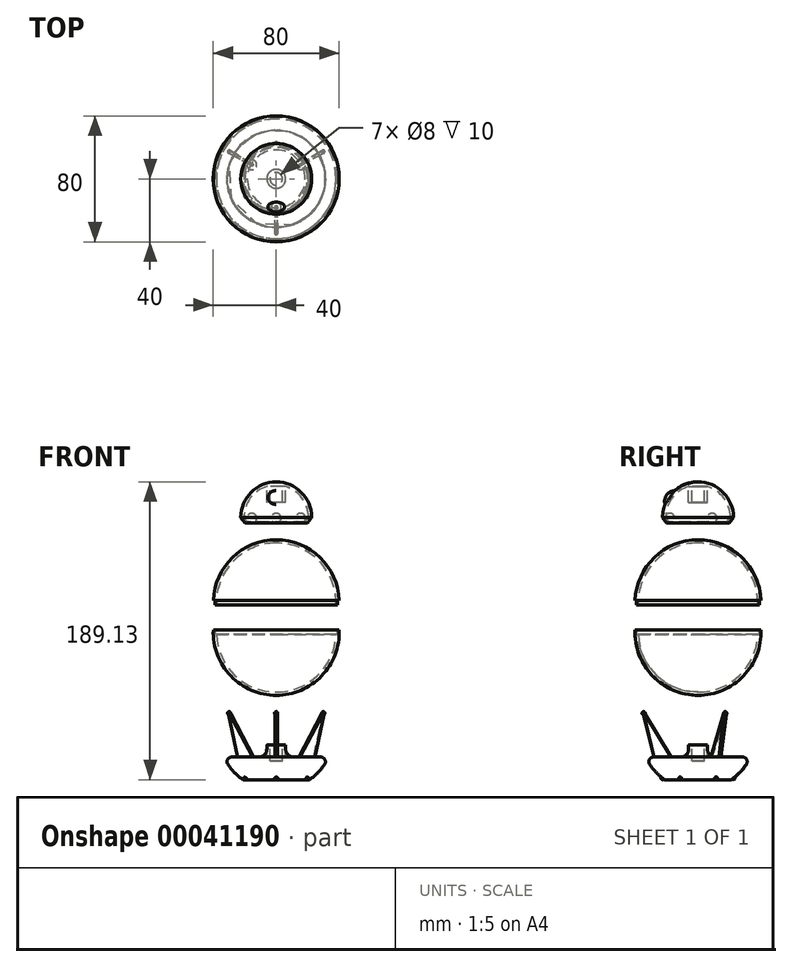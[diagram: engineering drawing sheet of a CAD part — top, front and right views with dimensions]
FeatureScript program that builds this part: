
annotation { "Feature Type Name" : "Feature", "Feature Type Description" : "" }
export const myFeature = defineFeature(function(context is Context, id is Id, definition is map)
    precondition{}
    {
        {
            var Q0;
            Q0=qCreatedBy(makeId("Right.planeOp"),FACE);
            var sketch = newSketch(context, id + "F0", { "sketchPlane" : qUnion([Q0])});
            skArc(sketch, "E0", {"start": v(0, 22.5) * mm, "mid": v(-15.9, 15.9) * mm, "end": v(-22.5, 0) * mm});
            skArc(sketch, "E1", {"start": v(-6, 19.6) * mm, "mid": v(-16.48, 12.2) * mm, "end": v(-20.5, 0) * mm});
            skLineSegment(sketch, "E2", {"start": v(-22.5, 0) * mm, "end": v(-19.9, -3.7) * mm});
            skLineSegment(sketch, "E3", {"start": v(-18.4, -3.01) * mm, "end": v(-20.5, 0) * mm});
            skLineSegment(sketch, "E4", {"start": v(0, 22.5) * mm, "end": v(0, 20.5) * mm});
            skPoint(sketch, "E5.start.orphan", {"position": v(22.5, 0) * mm});
            skCircle(sketch, "E6", {"center": v(0, -45.18) * mm, "radius": 45 * mm, "construction": true});
            skArc(sketch, "E7.0", {"start": v(-18.4, -3.01) * mm, "mid": v(-19.15, -3.35) * mm, "end": v(-19.9, -3.7) * mm});
            skLineSegment(sketch, "E8.bottom", {"start": v(0, 9.44) * mm, "end": v(-4, 9.44) * mm, "construction": true});
            skLineSegment(sketch, "E8.top", {"start": v(0, 19.44) * mm, "end": v(-4, 19.44) * mm, "construction": true});
            skLineSegment(sketch, "E8.left", {"start": v(0, 9.44) * mm, "end": v(0, 19.44) * mm, "construction": true});
            skLineSegment(sketch, "E8.right", {"start": v(-4, 9.44) * mm, "end": v(-4, 19.44) * mm, "construction": true});
            skLineSegment(sketch, "E9", {"start": v(-4, 9.44) * mm, "end": v(-4, 19.44) * mm});
            skLineSegment(sketch, "E10", {"start": v(0, 19.44) * mm, "end": v(0, 20.5) * mm});
            skLineSegment(sketch, "E11", {"start": v(-4, 9.44) * mm, "end": v(-6, 9.44) * mm});
            skLineSegment(sketch, "E12", {"start": v(-6, 9.44) * mm, "end": v(-6, 19.6) * mm});
            skLineSegment(sketch, "E13", {"start": v(-4, 19.44) * mm, "end": v(0, 19.44) * mm});
            skCircle(sketch, "E14", {"center": v(-17.9, -0.54) * mm, "radius": 3.1 * mm, "construction": true});
            skSolve(sketch);
        }
        {
            var Q0;
            Q0=qCreatedBy(makeId("Right.planeOp"),FACE);
            var sketch = newSketch(context, id + "F1", { "sketchPlane" : qUnion([Q0])});
            skLineSegment(sketch, "E15", {"start": v(0, 20.5) * mm, "end": v(0, 22.5) * mm});
            skArc(sketch, "E16", {"start": v(0, 22.5) * mm, "mid": v(-15.9, 15.9) * mm, "end": v(-22.5, 0) * mm});
            skArc(sketch, "E17", {"start": v(0, 20.5) * mm, "mid": v(-14.24, 14.75) * mm, "end": v(-20.49, 0.72) * mm});
            skLineSegment(sketch, "E18", {"start": v(-22.5, 0) * mm, "end": v(-19.1, -4) * mm});
            skLineSegment(sketch, "E19", {"start": v(-19.1, -4) * mm, "end": v(-17.58, -2.7) * mm});
            skLineSegment(sketch, "E20", {"start": v(-17.58, -2.7) * mm, "end": v(-20.5, 0.73) * mm});
            skPoint(sketch, "E21.end.orphan", {"position": v(-20.5, 0) * mm});
            skLineSegment(sketch, "E22", {"start": v(0, 22.5) * mm, "end": v(0, 20.5) * mm});
            skSolve(sketch);
        }
        {
            var Q0;
            Q0 = qSketchRegion(id + "F0", true);
            var Q1;
            Q1=sQuery(id+"F1.wireOp",EDGE,"E22");
            revolve(context, id + "F2", {"entities" : qUnion([Q0]), "axis" : qUnion([Q1]), "revolveType" : RevolveType.FULL});
        }
        {
            var Q0;
            Q0=qCreatedBy(makeId("Right.planeOp"),FACE);
            var sketch = newSketch(context, id + "F3", { "sketchPlane" : qUnion([Q0])});
            skArc(sketch, "E23.0", {"start": v(-14.81, -0.54) * mm, "mid": v(-17.9, 2.56) * mm, "end": v(-21, -0.54) * mm});
            skLineSegment(sketch, "E24", {"start": v(-17.9, -0.54) * mm, "end": v(-14.81, -0.54) * mm});
            skLineSegment(sketch, "E25", {"start": v(-14.81, -0.54) * mm, "end": v(-17.9, -0.54) * mm});
            skLineSegment(sketch, "E26", {"start": v(-17.9, -0.54) * mm, "end": v(-21, -0.54) * mm});
            skSolve(sketch);
        }
        {
            var Q0;
            Q0 = qSketchRegion(id + "F3", true);
            var Q1;
            Q1=sQuery(id+"F3.wireOp",EDGE,"E25");
            revolve(context, id + "F4", {"entities" : qUnion([Q0]), "axis" : qUnion([Q1]), "revolveType" : RevolveType.FULL});
        }
        {
            var Q0;
            Q0=makeQuery(id+"F4.opRevolve","SWEPT_BODY",BODY,{"disambiguationData":[OSD([sQuery(id+"F3.wireOp",EDGE,"E23.0"),sQuery(id+"F3.wireOp",EDGE,"E25"),sQuery(id+"F3.wireOp",EDGE,"E26")])]});
            var Q1;
            Q1=sQuery(id+"F0.wireOp",EDGE,"E8.left");
            circularPattern(context, id + "F5", {"entities" : qUnion([Q0]), "axis" : qUnion([Q1]), "angle" : 360 * degree, "instanceCount" : 3, "equalSpace" : true});
        }
        {
            var Q0;
            Q0=qCreatedBy(makeId("Right.planeOp"),FACE);
            var sketch = newSketch(context, id + "F6", { "sketchPlane" : qUnion([Q0])});
            skLineSegment(sketch, "E27", {"start": v(-17.2, 12.13) * mm, "end": v(-19.97, 14.1) * mm});
            skArc(sketch, "E28", {"start": v(-13.55, 16.9) * mm, "mid": v(-17.15, 16.4) * mm, "end": v(-19.97, 14.1) * mm});
            skPoint(sketch, "E29.orphan", {"position": v(-6, 19.6) * mm});
            skPoint(sketch, "E30.orphan", {"position": v(-20.5, 0) * mm});
            skLineSegment(sketch, "E31", {"start": v(-17.2, 12.13) * mm, "end": v(-13.55, 16.9) * mm});
            skLineSegment(sketch, "E32", {"start": v(-17.2, 12.13) * mm, "end": v(0, 0) * mm, "construction": true});
            skSolve(sketch);
        }
        {
            var Q0;
            Q0=makeQuery(id+"F6.imprint","IMPRINT",FACE,{"disambiguationData":[TD([[makeQuery(id+"F6.imprint","IMPRINT",EDGE,{"derivedFrom":sQuery(id+"F6.wireOp",EDGE,"E27")}),-1.0]])]});
            var Q1;
            Q1=sQuery(id+"F6.wireOp",EDGE,"E27");
            revolve(context, id + "F7", {"operationType" : NewBodyOperationType.ADD, "entities" : qUnion([Q0]), "axis" : qUnion([Q1]), "revolveType" : RevolveType.FULL});
        }
        {
            var Q0;
            Q0=qCreatedBy(makeId("Right.planeOp"),FACE);
            var sketch = newSketch(context, id + "F8", { "sketchPlane" : qUnion([Q0])});
            skArc(sketch, "E33", {"start": v(0, -14.3) * mm, "mid": v(-40, -54.3) * mm, "end": v(0, -94.3) * mm});
            skArc(sketch, "E34.0", {"start": v(0, -16.3) * mm, "mid": v(-38, -54.3) * mm, "end": v(0, -92.3) * mm});
            skArc(sketch, "E35.0", {"start": v(-38.97, -52.8) * mm, "mid": v(-39, -54.3) * mm, "end": v(-38.97, -55.8) * mm});
            skPoint(sketch, "E36.rect.right.end.orphan", {"position": v(-48.08, -52.8) * mm});
            skPoint(sketch, "E36.rect.right.start.orphan", {"position": v(-48.08, -55.8) * mm});
            skLineSegment(sketch, "E37.trimOffspring", {"start": v(-38.97, -52.8) * mm, "end": v(-39.97, -52.8) * mm});
            skLineSegment(sketch, "E38.trimOffspring", {"start": v(-37.97, -55.8) * mm, "end": v(-38.97, -55.8) * mm});
            skLineSegment(sketch, "E39", {"start": v(0, -14.3) * mm, "end": v(0, -16.3) * mm});
            skPoint(sketch, "E36.rect.left.end.orphan", {"position": v(48.08, -52.8) * mm});
            skPoint(sketch, "E36.rect.left.start.orphan", {"position": v(48.08, -55.8) * mm});
            skLineSegment(sketch, "E40.trimOffspring", {"start": v(0, -92.3) * mm, "end": v(0, -94.3) * mm});
            skSolve(sketch);
        }
        {
            var Q0;
            Q0=makeQuery(id+"F8.imprint","IMPRINT",FACE,{"disambiguationData":[TD([[makeQuery(id+"F8.imprint","IMPRINT",EDGE,{"derivedFrom":sQuery(id+"F8.wireOp",EDGE,"E35.0")}),1.0]])]});
            var Q1;
            Q1=sQuery(id+"F8.wireOp",EDGE,"E39");
            revolve(context, id + "F9", {"entities" : qUnion([Q0]), "axis" : qUnion([Q1]), "revolveType" : RevolveType.FULL});
        }
        {
            var Q0;
            Q0=makeQuery(id+"F8.imprint","IMPRINT",FACE,{"disambiguationData":[TD([[makeQuery(id+"F8.imprint","IMPRINT",EDGE,{"derivedFrom":sQuery(id+"F8.wireOp",EDGE,"E35.0")}),-1.0]])]});
            var Q1;
            Q1=sQuery(id+"F8.wireOp",EDGE,"E40.trimOffspring");
            revolve(context, id + "F10", {"entities" : qUnion([Q0]), "axis" : qUnion([Q1]), "revolveType" : RevolveType.FULL});
        }
        {
            var Q0;
            Q0=qCreatedBy(makeId("Right.planeOp"),FACE);
            var sketch = newSketch(context, id + "F11", { "sketchPlane" : qUnion([Q0])});
            skCircle(sketch, "E41", {"center": v(0, -136.3) * mm, "radius": 40 * mm, "construction": true});
            skCircle(sketch, "E42.0", {"center": v(0, -136.3) * mm, "radius": 38 * mm, "construction": true});
            skArc(sketch, "E43.0", {"start": v(-33.39, -152.24) * mm, "mid": v(-19.74, -167.59) * mm, "end": v(0, -173.3) * mm});
            skLineSegment(sketch, "E44", {"start": v(-33.39, -152.24) * mm, "end": v(-6, -152.24) * mm});
            skLineSegment(sketch, "E45", {"start": v(-6, -152.24) * mm, "end": v(-6, -144.58) * mm});
            skLineSegment(sketch, "E46", {"start": v(-6, -144.58) * mm, "end": v(-4, -144.58) * mm});
            skLineSegment(sketch, "E47", {"start": v(-4, -144.58) * mm, "end": v(-4, -154.58) * mm});
            skLineSegment(sketch, "E48", {"start": v(-4, -154.58) * mm, "end": v(0, -154.58) * mm});
            skLineSegment(sketch, "E49", {"start": v(0, -154.58) * mm, "end": v(0, -173.3) * mm});
            skSolve(sketch);
        }
        {
            var Q0;
            Q0 = qSketchRegion(id + "F11", true);
            var Q1;
            Q1=sQuery(id+"F11.wireOp",EDGE,"E49");
            revolve(context, id + "F12", {"entities" : qUnion([Q0]), "axis" : qUnion([Q1]), "revolveType" : RevolveType.FULL});
        }
        {
            var Q0;
            Q0=makeQuery(id+"F12.opRevolve","SWEPT_EDGE",EDGE,{"disambiguationData":[OSD([sQuery(id+"F11.wireOp",EDGE,"E43.0"),sQuery(id+"F11.wireOp",EDGE,"E44")])]});
            fillet(context, id + "F13", {"entities" : qUnion([Q0]), "radius" : 3 * mm, "tangentPropagation" : true, "allowEdgeOverflow" : false});
        }
        {
            var Q0;
            Q0=qCreatedBy(makeId("Right.planeOp"),FACE);
            var sketch = newSketch(context, id + "F14", { "sketchPlane" : qUnion([Q0])});
            skArc(sketch, "E50", {"start": v(-21.93, -164.84) * mm, "mid": v(-23.33, -165.02) * mm, "end": v(-23.15, -166.42) * mm});
            skLineSegment(sketch, "E51", {"start": v(-21.93, -164.84) * mm, "end": v(-23.15, -166.42) * mm});
            skPoint(sketch, "E52.orphan", {"position": v(0, -136.52) * mm});
            skSolve(sketch);
        }
        {
            var Q0;
            Q0=makeQuery(id+"F14.imprint","IMPRINT",FACE,{"disambiguationData":[TD([[makeQuery(id+"F14.imprint","IMPRINT",EDGE,{"derivedFrom":sQuery(id+"F14.wireOp",EDGE,"E50")}),1.0]])]});
            var Q1;
            Q1=sQuery(id+"F14.wireOp",EDGE,"E51");
            revolve(context, id + "F15", {"operationType" : NewBodyOperationType.ADD, "entities" : qUnion([Q0]), "axis" : qUnion([Q1]), "revolveType" : RevolveType.FULL});
        }
        {
            var Q0;
            Q0=makeQuery(id+"F12.opRevolve","SWEPT_BODY",BODY,{"disambiguationData":[OSD([sQuery(id+"F11.wireOp",EDGE,"E43.0"),sQuery(id+"F11.wireOp",EDGE,"E44"),sQuery(id+"F11.wireOp",EDGE,"E45"),sQuery(id+"F11.wireOp",EDGE,"E46"),sQuery(id+"F11.wireOp",EDGE,"E47"),sQuery(id+"F11.wireOp",EDGE,"E48"),sQuery(id+"F11.wireOp",EDGE,"E49")])]});
            var Q1;
            Q1=sQuery(id+"F11.wireOp",EDGE,"E49");
            circularPattern(context, id + "F16", {"entities" : qUnion([Q0]), "axis" : qUnion([Q1]), "angle" : 360 * degree, "instanceCount" : 6, "equalSpace" : true});
        }
        {
            var Q0;
            Q0=qCreatedBy(makeId("Right.planeOp"),FACE);
            var sketch = newSketch(context, id + "F17", { "sketchPlane" : qUnion([Q0])});
            skLineSegment(sketch, "E53.rect.bottom", {"start": v(77.76, -166.63) * mm, "end": v(-77.76, -166.63) * mm});
            skLineSegment(sketch, "E53.rect.top", {"start": v(77.76, -241.75) * mm, "end": v(-77.76, -241.75) * mm});
            skLineSegment(sketch, "E53.rect.left", {"start": v(77.76, -166.63) * mm, "end": v(77.76, -241.75) * mm});
            skLineSegment(sketch, "E53.rect.right", {"start": v(-77.76, -166.63) * mm, "end": v(-77.76, -241.75) * mm});
            skPoint(sketch, "E53.rect.middle", {"position": v(0, -204.2) * mm});
            skCircle(sketch, "E54", {"center": v(-22.54, -165.63) * mm, "radius": 1 * mm, "construction": true});
            skSolve(sketch);
        }
        {
            var Q0;
            Q0=makeQuery(id+"F17.imprint","IMPRINT",FACE,{"disambiguationData":[TD([[makeQuery(id+"F17.imprint","IMPRINT",EDGE,{"derivedFrom":sQuery(id+"F17.wireOp",EDGE,"E53.rect.bottom")}),1.0]])]});
            extrude(context, id + "F18", {"entities" : qUnion([Q0]), "operationType" : NewBodyOperationType.REMOVE, "endBound" : BoundingType.THROUGH_ALL, "oppositeDirection" : true, "depth" : 25 * mm, "hasSecondDirection" : true, "secondDirectionBound" : SecondDirectionBoundingType.THROUGH_ALL, "secondDirectionOppositeDirection" : false, "secondDirectionDepth" : 25 * mm});
        }
        {
            var Q0;
            Q0=qCreatedBy(makeId("Right.planeOp"),FACE);
            var sketch = newSketch(context, id + "F19", { "sketchPlane" : qUnion([Q0])});
            skLineSegment(sketch, "E55", {"start": v(-28.06, -152.24) * mm, "end": v(-34.56, -125.08) * mm});
            skLineSegment(sketch, "E56", {"start": v(-34.56, -125.08) * mm, "end": v(-33.72, -124.88) * mm});
            skLineSegment(sketch, "E57", {"start": v(-33.72, -124.88) * mm, "end": v(-17.06, -152.24) * mm});
            skLineSegment(sketch, "E58", {"start": v(-17.06, -152.24) * mm, "end": v(-28.06, -152.24) * mm});
            skSolve(sketch);
        }
        {
            var Q0;
            Q0=makeQuery(id+"F19.imprint","IMPRINT",FACE,{"disambiguationData":[TD([[makeQuery(id+"F19.imprint","IMPRINT",EDGE,{"derivedFrom":sQuery(id+"F19.wireOp",EDGE,"E55")}),-1.0]])]});
            var Q1;
            Q1=sQuery(id+"F11.wireOp",EDGE,"E49");
            revolve(context, id + "F20", {"entities" : qUnion([Q0]), "axis" : qUnion([Q1]), "revolveType" : RevolveType.SYMMETRIC, "angle" : 3 * degree});
        }
        {
            var Q0;
            Q0=qCreatedBy(makeId("Right.planeOp"),FACE);
            var sketch = newSketch(context, id + "F21", { "sketchPlane" : qUnion([Q0])});
            skLineSegment(sketch, "E59", {"start": v(-35.47, -124.11) * mm, "end": v(0, -136.3) * mm, "construction": true});
            skArc(sketch, "E60", {"start": v(-33.58, -124.76) * mm, "mid": v(-34.2, -123.5) * mm, "end": v(-35.47, -124.11) * mm});
            skLineSegment(sketch, "E61", {"start": v(-35.47, -124.11) * mm, "end": v(-33.58, -124.76) * mm});
            skCircle(sketch, "E62.0", {"center": v(0, -136.3) * mm, "radius": 37.5 * mm, "construction": true});
            skSolve(sketch);
        }
        {
            var Q0;
            Q0=makeQuery(id+"F21.imprint","IMPRINT",FACE,{"disambiguationData":[TD([[makeQuery(id+"F21.imprint","IMPRINT",EDGE,{"derivedFrom":sQuery(id+"F21.wireOp",EDGE,"E60")}),1.0]])]});
            var Q1;
            Q1=sQuery(id+"F21.wireOp",EDGE,"E61");
            revolve(context, id + "F22", {"operationType" : NewBodyOperationType.ADD, "entities" : qUnion([Q0]), "axis" : qUnion([Q1]), "revolveType" : RevolveType.FULL});
        }
        {
            var Q0;
            Q0=makeQuery(id+"F20.opRevolve","SWEPT_BODY",BODY,{"disambiguationData":[OSD([sQuery(id+"F19.wireOp",EDGE,"E55"),sQuery(id+"F19.wireOp",EDGE,"E56"),sQuery(id+"F19.wireOp",EDGE,"E57"),sQuery(id+"F19.wireOp",EDGE,"E58")])]});
            var Q1;
            Q1=sQuery(id+"F11.wireOp",EDGE,"E49");
            circularPattern(context, id + "F23", {"entities" : qUnion([Q0]), "axis" : qUnion([Q1]), "angle" : 360 * degree, "instanceCount" : 3, "equalSpace" : true});
        }
        {
            var Q0;
            Q0=makeQuery(id+"F20.opRevolve","CAP_EDGE",EDGE,{"disambiguationData":[OSD([sQuery(id+"F19.wireOp",EDGE,"E58")])],"isStart":true});
            var Q1;
            Q1=makeQuery(id+"F23.opPattern","COPY",EDGE,{"derivedFrom":makeQuery(id+"F20.opRevolve","CAP_EDGE",EDGE,{"disambiguationData":[OSD([sQuery(id+"F19.wireOp",EDGE,"E58")])],"isStart":false}),"instanceName":"1"});
            var Q2;
            Q2=makeQuery(id+"F23.opPattern","COPY",EDGE,{"derivedFrom":makeQuery(id+"F20.opRevolve","CAP_EDGE",EDGE,{"disambiguationData":[OSD([sQuery(id+"F19.wireOp",EDGE,"E58")])],"isStart":true}),"instanceName":"1"});
            var Q3;
            Q3=makeQuery(id+"F23.opPattern","COPY",EDGE,{"derivedFrom":makeQuery(id+"F20.opRevolve","CAP_EDGE",EDGE,{"disambiguationData":[OSD([sQuery(id+"F19.wireOp",EDGE,"E58")])],"isStart":false}),"instanceName":"2"});
            var Q4;
            Q4=makeQuery(id+"F23.opPattern","COPY",EDGE,{"derivedFrom":makeQuery(id+"F20.opRevolve","CAP_EDGE",EDGE,{"disambiguationData":[OSD([sQuery(id+"F19.wireOp",EDGE,"E58")])],"isStart":true}),"instanceName":"2"});
            var Q5;
            Q5=makeQuery(id+"F16.opPattern","COPY",EDGE,{"derivedFrom":makeQuery(id+"F12.opRevolve","SWEPT_EDGE",EDGE,{"disambiguationData":[OSD([sQuery(id+"F11.wireOp",EDGE,"E44"),sQuery(id+"F11.wireOp",EDGE,"E45")])]}),"instanceName":"4"});
            var Q6;
            Q6=makeQuery(id+"F20.opRevolve","CAP_EDGE",EDGE,{"disambiguationData":[OSD([sQuery(id+"F19.wireOp",EDGE,"E58")])],"isStart":false});
            var Q7;
            Q7=makeQuery(id+"F23.opPattern","COPY",EDGE,{"derivedFrom":makeQuery(id+"F20.opRevolve","SWEPT_EDGE",EDGE,{"disambiguationData":[OSD([sQuery(id+"F19.wireOp",EDGE,"E57"),sQuery(id+"F19.wireOp",EDGE,"E58")])]}),"instanceName":"2"});
            var Q8;
            Q8=makeQuery(id+"F23.opPattern","COPY",EDGE,{"derivedFrom":makeQuery(id+"F20.opRevolve","SWEPT_EDGE",EDGE,{"disambiguationData":[OSD([sQuery(id+"F19.wireOp",EDGE,"E57"),sQuery(id+"F19.wireOp",EDGE,"E58")])]}),"instanceName":"1"});
            var Q9;
            Q9=makeQuery(id+"F20.opRevolve","SWEPT_EDGE",EDGE,{"disambiguationData":[OSD([sQuery(id+"F19.wireOp",EDGE,"E57"),sQuery(id+"F19.wireOp",EDGE,"E58")])]});
            var Q10;
            Q10=makeQuery(id+"F20.opRevolve","SWEPT_EDGE",EDGE,{"disambiguationData":[OSD([sQuery(id+"F19.wireOp",EDGE,"E55"),sQuery(id+"F19.wireOp",EDGE,"E58")])]});
            var Q11;
            Q11=makeQuery(id+"F23.opPattern","COPY",EDGE,{"derivedFrom":makeQuery(id+"F20.opRevolve","SWEPT_EDGE",EDGE,{"disambiguationData":[OSD([sQuery(id+"F19.wireOp",EDGE,"E55"),sQuery(id+"F19.wireOp",EDGE,"E58")])]}),"instanceName":"2"});
            var Q12;
            Q12=makeQuery(id+"F23.opPattern","COPY",EDGE,{"derivedFrom":makeQuery(id+"F20.opRevolve","SWEPT_EDGE",EDGE,{"disambiguationData":[OSD([sQuery(id+"F19.wireOp",EDGE,"E55"),sQuery(id+"F19.wireOp",EDGE,"E58")])]}),"instanceName":"1"});
            fillet(context, id + "F24", {"entities" : qUnion([Q0, Q1, Q2, Q3, Q4, Q5, Q6, Q7, Q8, Q9, Q10, Q11, Q12]), "radius" : 5 * mm, "tangentPropagation" : true, "allowEdgeOverflow" : false});
        }
        {
            var Q0;
            Q0=makeQuery(id+"F10.opRevolve","SWEPT_BODY",BODY,{"disambiguationData":[OSD([sQuery(id+"F8.wireOp",EDGE,"E33"),sQuery(id+"F8.wireOp",EDGE,"E34.0"),sQuery(id+"F8.wireOp",EDGE,"E35.0"),sQuery(id+"F8.wireOp",EDGE,"E37.trimOffspring"),sQuery(id+"F8.wireOp",EDGE,"E38.trimOffspring"),sQuery(id+"F8.wireOp",EDGE,"E40.trimOffspring")])]});
            var Q1;
            Q1=sQuery(id+"F11.wireOp",EDGE,"E49");
            transform(context, id + "F25", {"entities" : qUnion([Q0]), "transformType" : TransformType.TRANSLATION_ENTITY, "oppositeDirectionEntity" : false, "transformLine" : qUnion([Q1]), "makeCopy" : false});
        }
    });
